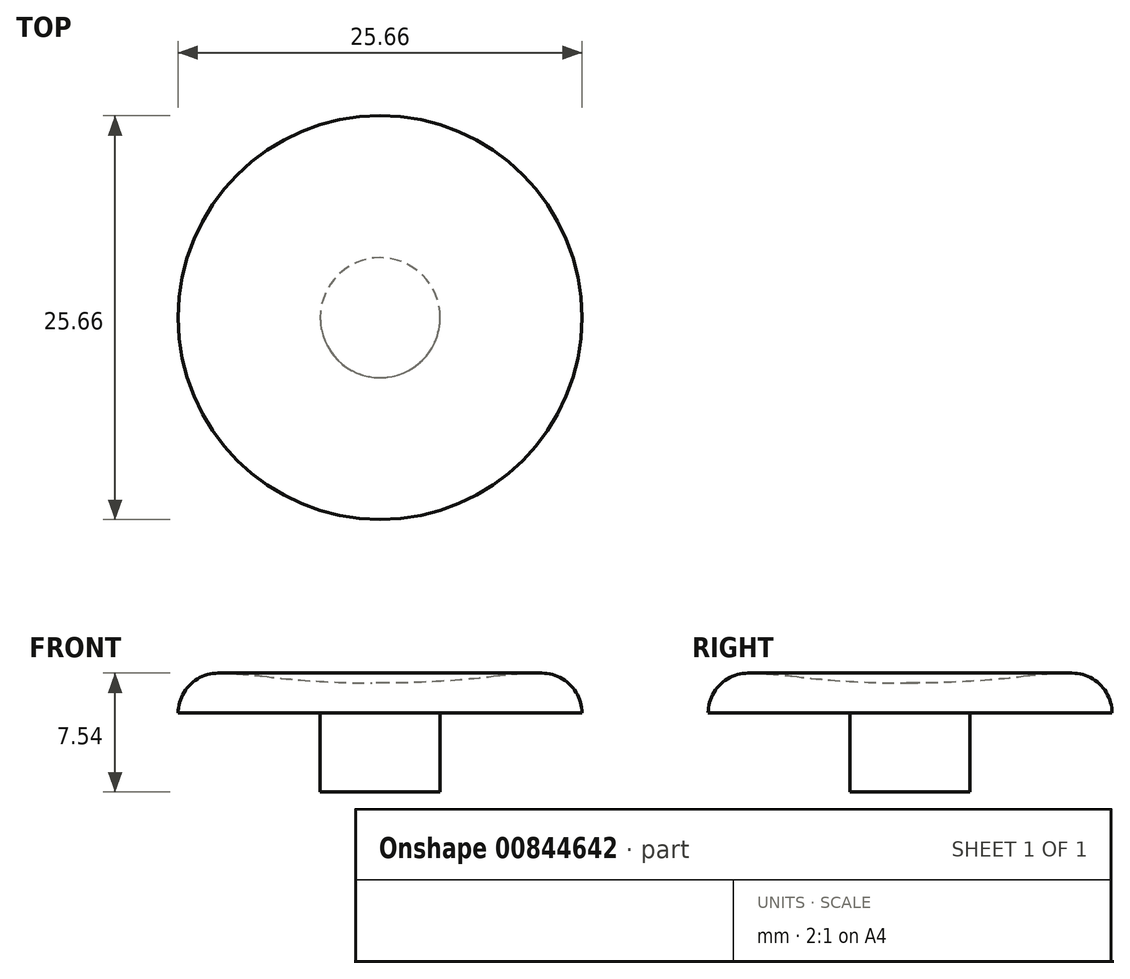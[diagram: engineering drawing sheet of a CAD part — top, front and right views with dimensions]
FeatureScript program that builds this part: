
annotation { "Feature Type Name" : "Feature", "Feature Type Description" : "" }
export const myFeature = defineFeature(function(context is Context, id is Id, definition is map)
    precondition{}
    {
        {
            var Q0;
            Q0=qCreatedBy(makeId("Top.planeOp"),FACE);
            var sketch = newSketch(context, id + "F0", { "sketchPlane" : qUnion([Q0])});
            skCircle(sketch, "E0", {"center": v(0, 0) * mm, "radius": 12.83 * mm});
            skSolve(sketch);
        }
        {
            var Q0;
            Q0=makeQuery(id+"F0.imprint","IMPRINT",FACE,{"disambiguationData":[TD([[makeQuery(id+"F0.imprint","IMPRINT",EDGE,{"derivedFrom":sQuery(id+"F0.wireOp",EDGE,"E0")}),1.0]])]});
            extrude(context, id + "F1", {"entities" : qUnion([Q0]), "depth" : 2.54 * mm, "offsetDistance" : 25.4 * mm});
        }
        {
            var Q0;
            Q0=makeQuery(id+"F1.opExtrude","CAP_FACE",FACE,{"disambiguationData":[OSD([sQuery(id+"F0.wireOp",EDGE,"E0")])],"isStart":false});
            var sketch = newSketch(context, id + "F2", { "sketchPlane" : qUnion([Q0])});
            skCircle(sketch, "E1", {"center": v(0, 0) * mm, "radius": 8.9 * mm});
            skSolve(sketch);
        }
        {
            var Q0;
            Q0=makeQuery(id+"F2.imprint","IMPRINT",FACE,{"disambiguationData":[TD([[makeQuery(id+"F2.imprint","IMPRINT",EDGE,{"derivedFrom":sQuery(id+"F2.wireOp",EDGE,"E1")}),1.0]])]});
            extrude(context, id + "F3", {"entities" : qUnion([Q0]), "operationType" : NewBodyOperationType.REMOVE, "oppositeDirection" : true, "depth" : 0.64 * mm, "offsetDistance" : 25.4 * mm});
        }
        {
            var Q0;
            Q0=makeQuery(id+"F3.boolean.opBoolean","COPY",EDGE,{"derivedFrom":makeQuery(id+"F3.opExtrude","CAP_EDGE",EDGE,{"disambiguationData":[OSD([sQuery(id+"F2.wireOp",EDGE,"E1")])],"isStart":false})});
            fillet(context, id + "F4", {"entities" : qUnion([Q0]), "radius" : 60.96 * mm, "tangentPropagation" : true, "allowEdgeOverflow" : false});
        }
        {
            var Q0;
            Q0=makeQuery(id+"F4.opFillet","BLEND_EDGE",EDGE,{"blendedFrom":[makeQuery(id+"F3.boolean.opBoolean","COPY",EDGE,{"derivedFrom":makeQuery(id+"F3.opExtrude","CAP_EDGE",EDGE,{"disambiguationData":[OSD([sQuery(id+"F2.wireOp",EDGE,"E1")])],"isStart":false})}),makeQuery(id+"F1.opExtrude","CAP_FACE",FACE,{"disambiguationData":[OSD([sQuery(id+"F0.wireOp",EDGE,"E0")])],"isStart":false})],"blendedInto":[makeQuery(id+"F1.opExtrude","CAP_FACE",FACE,{"disambiguationData":[OSD([sQuery(id+"F0.wireOp",EDGE,"E0")])],"isStart":false})]});
            fillet(context, id + "F5", {"entities" : qUnion([Q0]), "radius" : 25.4 * mm, "tangentPropagation" : true, "allowEdgeOverflow" : false});
        }
        {
            var Q0;
            Q0=makeQuery(id+"F1.opExtrude","CAP_EDGE",EDGE,{"disambiguationData":[OSD([sQuery(id+"F0.wireOp",EDGE,"E0")])],"isStart":false});
            fillet(context, id + "F6", {"entities" : qUnion([Q0]), "radius" : 2.54 * mm, "tangentPropagation" : true, "allowEdgeOverflow" : false});
        }
        {
            var Q0;
            Q0=makeQuery(id+"F1.opExtrude","CAP_FACE",FACE,{"disambiguationData":[OSD([sQuery(id+"F0.wireOp",EDGE,"E0")])],"isStart":true});
            var sketch = newSketch(context, id + "F7", { "sketchPlane" : qUnion([Q0])});
            skCircle(sketch, "E2", {"center": v(0, 0) * mm, "radius": 3.81 * mm});
            skSolve(sketch);
        }
        {
            var Q0;
            Q0=makeQuery(id+"F7.imprint","IMPRINT",FACE,{"disambiguationData":[TD([[makeQuery(id+"F7.imprint","IMPRINT",EDGE,{"derivedFrom":sQuery(id+"F7.wireOp",EDGE,"E2")}),1.0]])]});
            extrude(context, id + "F8", {"entities" : qUnion([Q0]), "operationType" : NewBodyOperationType.ADD, "depth" : 5 * mm, "offsetDistance" : 25.4 * mm});
        }
    });
